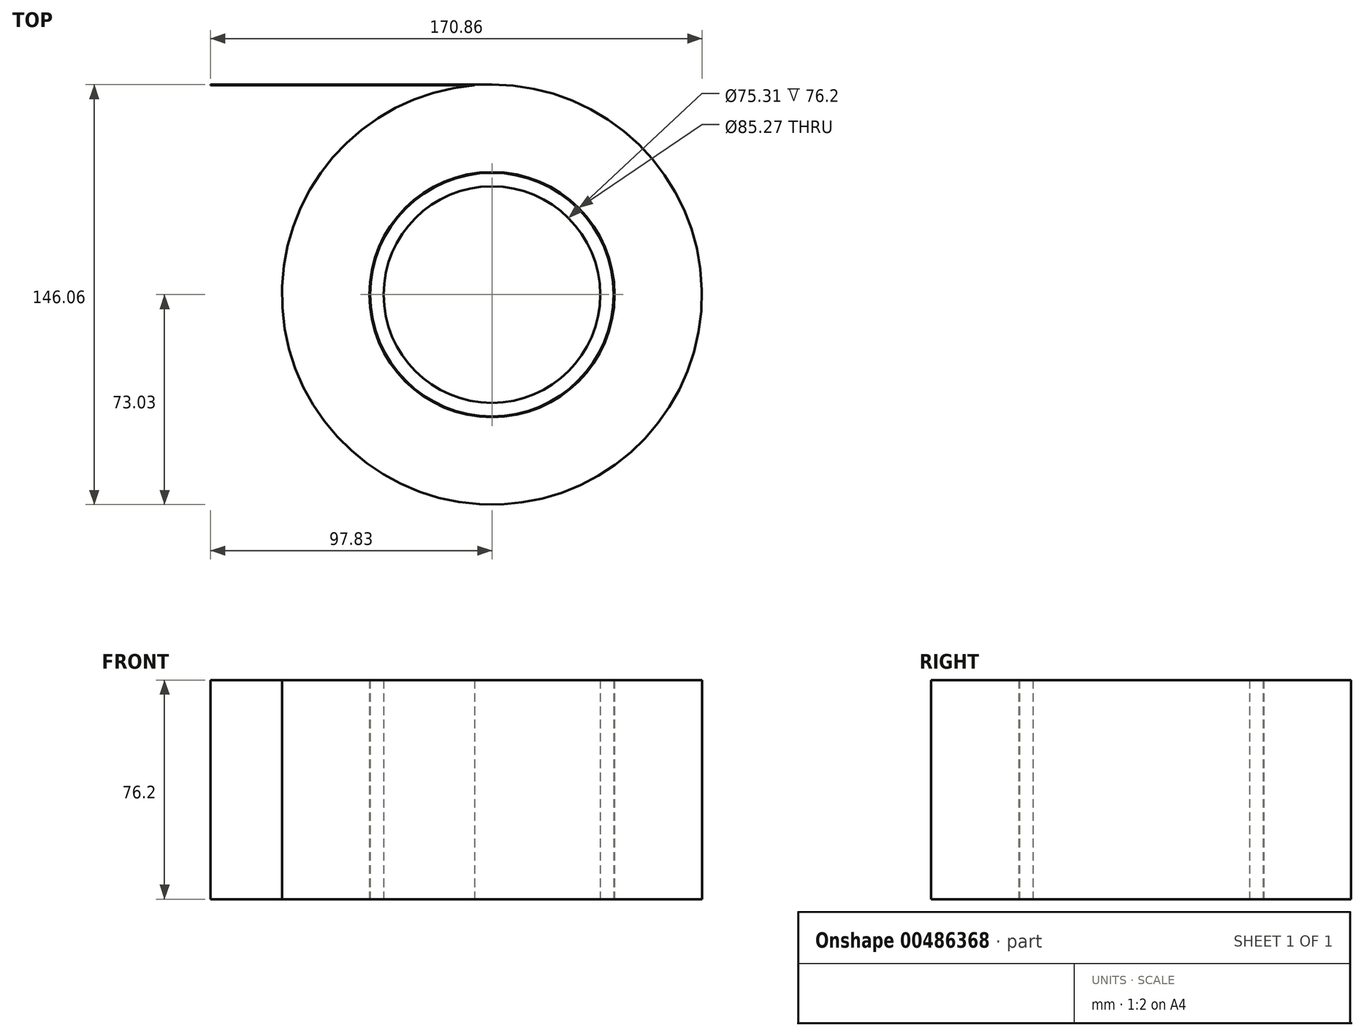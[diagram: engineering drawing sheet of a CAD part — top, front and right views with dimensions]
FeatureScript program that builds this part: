
annotation { "Feature Type Name" : "Feature", "Feature Type Description" : "" }
export const myFeature = defineFeature(function(context is Context, id is Id, definition is map)
    precondition{}
    {
        {
            var Q0;
            Q0=qCreatedBy(makeId("Top.planeOp"),FACE);
            var sketch = newSketch(context, id + "F0", { "sketchPlane" : qUnion([Q0])});
            skCircle(sketch, "E0", {"center": v(0, 0) * mm, "radius": 73.03 * mm});
            skCircle(sketch, "E1", {"center": v(0, 0) * mm, "radius": 42.64 * mm});
            skCircle(sketch, "E2", {"center": v(0, 0) * mm, "radius": 40.5 * mm});
            skSolve(sketch);
        }
        {
            var Q0;
            Q0 = qSketchRegion(id + "F0", true);
            extrude(context, id + "F1", {"entities" : qUnion([Q0]), "depth" : 76.2 * mm});
        }
        {
            var Q0;
            Q0=qCreatedBy(makeId("Top.planeOp"),FACE);
            var sketch = newSketch(context, id + "F2", { "sketchPlane" : qUnion([Q0])});
            skCircle(sketch, "E3", {"center": v(0, 0) * mm, "radius": 37.66 * mm});
            skCircle(sketch, "E4", {"center": v(0, 0) * mm, "radius": 42.35 * mm});
            skSolve(sketch);
        }
        {
            var Q0;
            Q0 = qSketchRegion(id + "F2", true);
            extrude(context, id + "F3", {"entities" : qUnion([Q0]), "depth" : 76.2 * mm});
        }
        {
            var Q0;
            Q0=qCreatedBy(makeId("Front.planeOp"),FACE);
            cPlane(context, id + "F4", {"entities" : qUnion([Q0]), "cplaneType" : CPlaneType.OFFSET, "offset" : 73.02 * mm, "oppositeDirection" : true, "width" : 152.4 * mm, "height" : 152.4 * mm});
        }
        {
            var Q0;
            Q0=qCreatedBy(id+"F4.planeOp",FACE);
            var sketch = newSketch(context, id + "F5", { "sketchPlane" : qUnion([Q0])});
            skLineSegment(sketch, "E5", {"start": v(0, 0) * mm, "end": v(-97.83, 0) * mm});
            skLineSegment(sketch, "E6.0", {"start": v(-73.03, 76.2) * mm, "end": v(0, 76.2) * mm});
            skLineSegment(sketch, "E7", {"start": v(0, 0) * mm, "end": v(0, 76.2) * mm});
            skLineSegment(sketch, "E8", {"start": v(-73.03, 76.2) * mm, "end": v(-97.83, 76.2) * mm});
            skLineSegment(sketch, "E9", {"start": v(-97.83, 76.2) * mm, "end": v(-97.83, 0) * mm});
            skPoint(sketch, "E10.orphan", {"position": v(73.03, 76.2) * mm});
            skSolve(sketch);
        }
        {
            var Q0;
            Q0=makeQuery(id+"F5.imprint","IMPRINT",FACE,{"disambiguationData":[TD([[makeQuery(id+"F5.imprint","IMPRINT",EDGE,{"derivedFrom":sQuery(id+"F5.wireOp",EDGE,"E5")}),-1.0]])]});
            extrude(context, id + "F6", {"entities" : qUnion([Q0]), "operationType" : NewBodyOperationType.ADD, "depth" : 0.25 * mm});
        }
    });
